FCSTD DOCUMENT  (FreeCAD 1.0R38641 +468 (Git))
Label: 03deltabot_assembly
License: All rights reserved
LicenseURL: https://en.wikipedia.org/wiki/All_rights_reserved
objects: App::FeaturePython×31, App::Link×23, Assembly::JointGroup×1, Assembly::AssemblyObject×1
EXTERNAL_REF file=01main.FCStd obj=Body004
EXTERNAL_REF file=01main.FCStd obj=Body006
EXTERNAL_REF file=01main.FCStd obj=Body007
EXTERNAL_REF file=stepper-motor-nema-23-57bygh201-1.snapshot.3/nema23.FCStd obj=Fusion001
EXTERNAL_REF file=01main.FCStd obj=Body008
EXTERNAL_REF file=si8t-k-rod-end-bearing-1.snapshot.1/8mm_rodend.FCStd obj=Part__Feature
EXTERNAL_REF file=01main.FCStd obj=Body
EXTERNAL_REF file=01main.FCStd obj=Body009

FEATURE [App::Link] base_triangle
  LinkedObject = -> <external 01main.FCStd>#Body004
FEATURE [App::FeaturePython] GroundedJoint  # Assembly grounded joint (typed FeaturePython)
  ObjectToGround = -> base_triangle
FEATURE [App::Link] vslot
  LinkPlacement = pos=(-30.6697,-27.5,-10.5) rot=(0,1,0;1.5708rad)
  LinkedObject = -> <external 01main.FCStd>#Body006
  Placement = pos=(-30.6697,-27.5,-10.5) rot=(0,1,0;1.5708rad)
FEATURE [App::FeaturePython] Joint  label="Slider"  # Assembly joint (typed FeaturePython)
  Activated = true
  AngleMax = 0
  AngleMin = 0
  Detach1 = false
  Detach2 = false
  Distance = 0
  Distance2 = 0
  EnableAngleMax = false
  EnableAngleMin = false
  EnableLengthMax = false
  EnableLengthMin = false
  JointType = 3 (Slider)
  LengthMax = 0
  LengthMin = 0
  Offset1 = pos=(-2,0,77) rot=(0,0,1;0rad)
  Offset2 = pos=(0,0,0) rot=(0,0,1;3.14159rad)
  Placement1 = pos=(-10.5,-10,180.895) rot=(0,0,1;0rad)
  Placement2 = pos=(1.22e-14,-37.5,0) rot=(0,-1,0;4.71239rad)
  Reference1 = -> Assembly [vslot.Edge5,vslot.Edge5]
  Reference2 = -> Assembly [base_triangle.Edge6,base_triangle.Edge6]
FEATURE [App::Link] nema23_holder
  LinkPlacement = pos=(145.212,-12,-49.5) rot=(1,0,0;1.5708rad)
  LinkedObject = -> <external 01main.FCStd>#Body007
  Placement = pos=(145.212,-12,-49.5) rot=(1,0,0;1.5708rad)
FEATURE [App::FeaturePython] Joint001  label="Slider001"  # Assembly joint (typed FeaturePython)
  Activated = true
  AngleMax = 0
  AngleMin = 0
  Detach1 = false
  Detach2 = false
  Distance = 0
  Distance2 = 0
  EnableAngleMax = false
  EnableAngleMin = false
  EnableLengthMax = false
  EnableLengthMin = false
  JointType = 3 (Slider)
  LengthMax = 0
  LengthMin = 0
  Offset1 = pos=(-2,-3,-72) rot=(0,0,1;0rad)
  Offset2 = pos=(0,0,0) rot=(0,0,1;1.5708rad)
  Placement1 = pos=(72,49,7) rot=(-0.707107,0,0.707107;3.14159rad)
  Placement2 = pos=(-10,8.5,103.895) rot=(0,0,1;1.5708rad)
  Reference1 = -> Assembly [nema23_holder.Edge21,nema23_holder.Edge21]
  Reference2 = -> Assembly [vslot.Edge113,vslot.Edge113]
FEATURE [App::Link] Fusion001
  LinkPlacement = pos=(145.212,-17,-49.5) rot=(1,0,0;4.71239rad)
  LinkedObject = -> <external stepper-motor-nema-23-57bygh201-1.snapshot.3/nema23.FCStd>#Fusion001
  Placement = pos=(145.212,-17,-49.5) rot=(1,0,0;4.71239rad)
FEATURE [App::FeaturePython] Joint002  label="Fixed"  # Assembly joint (typed FeaturePython)
  Activated = true
  AngleMax = 0
  AngleMin = 0
  Detach1 = false
  Detach2 = false
  Distance = 0
  Distance2 = 0
  EnableAngleMax = false
  EnableAngleMin = false
  EnableLengthMax = false
  EnableLengthMin = false
  JointType = 0 (Fixed)
  LengthMax = 0
  LengthMin = 0
  Placement1 = pos=(2.84e-14,0,5) rot=(0,0,1;0rad)
  Reference1 = -> Assembly [nema23_holder.Edge25,nema23_holder.Edge25]
  Reference2 = -> Assembly [Fusion001.Edge2256,Fusion001.Edge2256]
FEATURE [App::Link] bicep001
  LinkPlacement = pos=(145.212,-6,-49.5) rot=(0.724362,0.487494,0.487494;4.39537rad)
  LinkedObject = -> <external 01main.FCStd>#Body008
  Placement = pos=(145.212,-6,-49.5) rot=(0.724362,0.487494,0.487494;4.39537rad)
FEATURE [App::FeaturePython] Joint003  label="Revolute"  # Assembly joint (typed FeaturePython)
  Activated = true
  AngleMax = 34.3
  AngleMin = -61.59
  Detach1 = false
  Detach2 = false
  Distance = 0
  Distance2 = 0
  EnableAngleMax = false
  EnableAngleMin = false
  EnableLengthMax = false
  EnableLengthMin = false
  JointType = 1 (Revolute)
  LengthMax = 0
  LengthMin = 0
  Placement1 = pos=(0,7.1e-15,21) rot=(-1,0,0;3.14159rad)
  Placement2 = pos=(2.84e-14,0,10) rot=(0,0,1;0rad)
  Reference1 = -> Assembly [Fusion001.Edge2765,Fusion001.Edge2765]
  Reference2 = -> Assembly [bicep001.Edge21,bicep001.Edge21]
FEATURE [App::Link] vslot001
  LinkPlacement = pos=(0.572518,-1.79163,20) rot=(0.935113,0.250563,0.250563;1.63783rad)
  LinkedObject = -> <external 01main.FCStd>#Body006
  Placement = pos=(0.572518,-1.79163,20) rot=(0.935113,0.250563,0.250563;1.63783rad)
FEATURE [App::FeaturePython] Joint004  label="Slider002"  # Assembly joint (typed FeaturePython)
  Activated = true
  AngleMax = 0
  AngleMin = 0
  Detach1 = false
  Detach2 = false
  Distance = 0
  Distance2 = 0
  EnableAngleMax = false
  EnableAngleMin = false
  EnableLengthMax = false
  EnableLengthMin = false
  JointType = 3 (Slider)
  LengthMax = 0
  LengthMin = 0
  Offset1 = pos=(3,0,0) rot=(0,0,1;0rad)
  Offset2 = pos=(0,0,0) rot=(0,0,1;3.14159rad)
  Placement1 = pos=(5.77241,-20.9981,0) rot=(0.186157,-0.694747,0.694747;3.50969rad)
  Placement2 = pos=(-5.1,-10,103.895) rot=(0,0,1;3.14159rad)
  Reference1 = -> Assembly [base_triangle.Sketch020.Edge10,base_triangle.Sketch020.Edge10]
  Reference2 = -> Assembly [vslot001.Edge8,vslot001.Edge8]
FEATURE [App::Link] vslot002
  LinkPlacement = pos=(108.165,188.547,20) rot=(0.935113,-0.250563,-0.250563;1.63783rad)
  LinkedObject = -> <external 01main.FCStd>#Body006
  Placement = pos=(108.165,188.547,20) rot=(0.935113,-0.250563,-0.250563;1.63783rad)
FEATURE [App::FeaturePython] Joint005  label="Slider003"  # Assembly joint (typed FeaturePython)
  Activated = true
  AngleMax = 0
  AngleMin = 0
  Detach1 = false
  Detach2 = false
  Distance = 0
  Distance2 = 0
  EnableAngleMax = false
  EnableAngleMin = false
  EnableLengthMax = false
  EnableLengthMin = false
  JointType = 3 (Slider)
  LengthMax = 0
  LengthMin = 0
  Offset1 = pos=(0,-2,0) rot=(0,0,1;0rad)
  Placement1 = pos=(3.1,-10,103.895) rot=(0,0,1;0rad)
  Placement2 = pos=(12.7006,16.9981,0) rot=(-0.935113,0.250563,-0.250563;1.63783rad)
  Reference1 = -> Assembly [vslot002.Edge32,vslot002.Edge32]
  Reference2 = -> Assembly [base_triangle.Sketch020.Edge14,base_triangle.Sketch020.Edge14]
FEATURE [App::Link] vslot003
  LinkPlacement = pos=(-10.6404,0.6,21) rot=(0,1,0;4.71239rad)
  LinkedObject = -> <external 01main.FCStd>#Body006
  Placement = pos=(-10.6404,0.6,21) rot=(0,1,0;4.71239rad)
FEATURE [App::FeaturePython] Joint006  label="Slider004"  # Assembly joint (typed FeaturePython)
  Activated = true
  AngleMax = 0
  AngleMin = 0
  Detach1 = false
  Detach2 = false
  Distance = 0
  Distance2 = 0
  EnableAngleMax = false
  EnableAngleMin = false
  EnableLengthMax = false
  EnableLengthMin = false
  JointType = 3 (Slider)
  LengthMax = 0
  LengthMin = 0
  Offset1 = pos=(-3,0,0) rot=(0,0,1;0rad)
  Placement1 = pos=(-11,-3.1,103.895) rot=(0,0,1;0rad)
  Placement2 = pos=(-21.0711,-2.5,0) rot=(0.707107,0,0.707107;3.14159rad)
  Reference1 = -> Assembly [vslot003.Edge140,vslot003.Edge140]
  Reference2 = -> Assembly [base_triangle.Sketch020.Edge6,base_triangle.Sketch020.Edge6]
FEATURE [App::Link] vslot004
  LinkPlacement = pos=(110.289,-190.084,29.8935) rot=(0.965926,0.258819,0;3.14159rad)
  LinkedObject = -> <external 01main.FCStd>#Body006
  Placement = pos=(110.289,-190.084,29.8935) rot=(0.965926,0.258819,0;3.14159rad)
FEATURE [App::FeaturePython] Joint007  label="Perpendicular"  # Assembly joint (typed FeaturePython)
  Activated = true
  AngleMax = 0
  AngleMin = 0
  Detach1 = false
  Detach2 = false
  Distance = 0
  Distance2 = 0
  EnableAngleMax = false
  EnableAngleMin = false
  EnableLengthMax = false
  EnableLengthMin = false
  JointType = 7 (Perpendicular)
  LengthMax = 0
  LengthMin = 0
  Placement1 = pos=(6.8,-10,103.895) rot=(-1,0,0;1.5708rad)
  Placement2 = pos=(1.12e-14,-1.78e-14,207.79) rot=(0,0,1;0rad)
  Reference1 = -> Assembly [vslot004.Face13,vslot004.Face13]
  Reference2 = -> Assembly [vslot001.Face50,vslot001.Face50]
FEATURE [App::FeaturePython] GroundedJoint002  # Assembly grounded joint (typed FeaturePython)
  ObjectToGround = -> vslot001
FEATURE [App::Link] vslot005
  LinkPlacement = pos=(113.296,196.756,-177.874) rot=(0,0,1;4.18879rad)
  LinkedObject = -> <external 01main.FCStd>#Body006
  Placement = pos=(113.296,196.756,-177.874) rot=(0,0,1;4.18879rad)
FEATURE [App::FeaturePython] Joint008  label="Perpendicular001"  # Assembly joint (typed FeaturePython)
  Activated = true
  AngleMax = 0
  AngleMin = 0
  Detach1 = false
  Detach2 = false
  Distance = 0
  Distance2 = 0
  EnableAngleMax = false
  EnableAngleMin = false
  EnableLengthMax = false
  EnableLengthMin = false
  JointType = 7 (Perpendicular)
  LengthMax = 0
  LengthMin = 0
  Placement1 = pos=(4,0,103.895) rot=(0.57735,0.57735,-0.57735;4.18879rad)
  Reference1 = -> Assembly [vslot005.Face20,vslot005.Face20]
  Reference2 = -> Assembly [vslot002.Face49,vslot002.Face49]
FEATURE [App::FeaturePython] GroundedJoint003  # Assembly grounded joint (typed FeaturePython)
  ObjectToGround = -> vslot005
FEATURE [App::FeaturePython] GroundedJoint004  # Assembly grounded joint (typed FeaturePython)
  ObjectToGround = -> vslot002
FEATURE [App::FeaturePython] GroundedJoint005  # Assembly grounded joint (typed FeaturePython)
  ObjectToGround = -> vslot004
FEATURE [App::Link] vslot006
  LinkPlacement = pos=(-227.958,0.367079,-176.934) rot=(0,0,1;0rad)
  LinkedObject = -> <external 01main.FCStd>#Body006
  Placement = pos=(-227.958,0.367079,-176.934) rot=(0,0,1;0rad)
FEATURE [App::FeaturePython] GroundedJoint006  # Assembly grounded joint (typed FeaturePython)
  ObjectToGround = -> vslot006
FEATURE [App::Link] vslot007
  LinkPlacement = pos=(32.9973,-15.153,-11.7272) rot=(-0.186157,0.694747,0.694747;3.50969rad)
  LinkedObject = -> <external 01main.FCStd>#Body006
  Placement = pos=(32.9973,-15.153,-11.7272) rot=(-0.186157,0.694747,0.694747;3.50969rad)
FEATURE [App::FeaturePython] Joint009  label="Slider005"  # Assembly joint (typed FeaturePython)
  Activated = true
  AngleMax = 0
  AngleMin = 0
  Detach1 = false
  Detach2 = false
  Distance = 0
  Distance2 = 0
  EnableAngleMax = false
  EnableAngleMin = false
  EnableLengthMax = false
  EnableLengthMin = false
  JointType = 3 (Slider)
  LengthMax = 0
  LengthMin = 0
  Offset1 = pos=(0,9,-76) rot=(0,0,1;0rad)
  Placement1 = pos=(-15.4861,76.8227,-9) rot=(0.186157,-0.694747,0.694747;3.50969rad)
  Placement2 = pos=(-4,2.72721,103.895) rot=(0,0,1;0rad)
  Reference1 = -> Assembly [base_triangle.Edge39,base_triangle.Edge39]
  Reference2 = -> Assembly [vslot007.Edge128,vslot007.Edge128]
FEATURE [App::Link] vslot008
  LinkPlacement = pos=(-12.304,36.6889,-10.2728) rot=(0.935113,-0.250563,-0.250563;1.63783rad)
  LinkedObject = -> <external 01main.FCStd>#Body006
  Placement = pos=(-12.304,36.6889,-10.2728) rot=(0.935113,-0.250563,-0.250563;1.63783rad)
FEATURE [App::FeaturePython] Joint010  label="Slider006"  # Assembly joint (typed FeaturePython)
  Activated = true
  AngleMax = 0
  AngleMin = 0
  Detach1 = false
  Detach2 = false
  Distance = 0
  Distance2 = 0
  EnableAngleMax = false
  EnableAngleMin = false
  EnableLengthMax = false
  EnableLengthMin = false
  JointType = 3 (Slider)
  LengthMax = 0
  LengthMin = 0
  Offset1 = pos=(0,13,-80) rot=(0,0,1;0rad)
  Placement1 = pos=(4,10.2728,23.895) rot=(0,0,1;0rad)
  Placement2 = pos=(-20.7874,13.9952,0) rot=(-0.935113,0.250563,-0.250563;1.63783rad)
  Reference1 = -> Assembly [vslot008.Edge56,vslot008.Edge56]
  Reference2 = -> Assembly [base_triangle.Edge30,base_triangle.Edge30]
FEATURE [App::Link] nema23_holder001
  LinkPlacement = pos=(-63.6967,132.326,-49.2272) rot=(0.774597,-0.447214,-0.447214;1.82348rad)
  LinkedObject = -> <external 01main.FCStd>#Body007
  Placement = pos=(-63.6967,132.326,-49.2272) rot=(0.774597,-0.447214,-0.447214;1.82348rad)
FEATURE [App::FeaturePython] Joint011  label="Slider007"  # Assembly joint (typed FeaturePython)
  Activated = true
  AngleMax = 0
  AngleMin = 0
  Detach1 = false
  Detach2 = false
  Distance = 0
  Distance2 = 0
  EnableAngleMax = false
  EnableAngleMin = false
  EnableLengthMax = false
  EnableLengthMin = false
  JointType = 3 (Slider)
  LengthMax = 0
  LengthMin = 0
  Offset2 = pos=(0,0,0) rot=(0,0,1;3.14159rad)
  Placement1 = pos=(10,8.5,103.895) rot=(0,0,1;0rad)
  Placement2 = pos=(2.84e-14,46,5.3e-15) rot=(0,1,0;4.71239rad)
  Reference1 = -> Assembly [vslot007.Edge74,vslot007.Edge74]
  Reference2 = -> Assembly [nema23_holder001.Edge6,nema23_holder001.Edge6]
FEATURE [App::Link] nema23_holder002
  LinkPlacement = pos=(-91.6035,-120.662,-47.7728) rot=(0.774597,0.447214,0.447214;1.82348rad)
  LinkedObject = -> <external 01main.FCStd>#Body007
  Placement = pos=(-91.6035,-120.662,-47.7728) rot=(0.774597,0.447214,0.447214;1.82348rad)
FEATURE [App::FeaturePython] Joint012  label="Slider008"  # Assembly joint (typed FeaturePython)
  Activated = true
  AngleMax = 0
  AngleMin = 0
  Detach1 = false
  Detach2 = false
  Distance = 0
  Distance2 = 0
  EnableAngleMax = false
  EnableAngleMin = false
  EnableLengthMax = false
  EnableLengthMin = false
  JointType = 3 (Slider)
  LengthMax = 0
  LengthMin = 0
  Offset2 = pos=(0,0,0) rot=(0,0,1;3.14159rad)
  Placement1 = pos=(10,8.5,103.895) rot=(0,0,1;0rad)
  Placement2 = pos=(2.84e-14,46,0) rot=(0,1,0;4.71239rad)
  Reference1 = -> Assembly [vslot008.Edge74,vslot008.Edge74]
  Reference2 = -> Assembly [nema23_holder002.Edge6,nema23_holder002.Edge6]
FEATURE [App::Link] Fusion002
  LinkPlacement = pos=(-63.6967,132.326,-49.2272) rot=(0.774597,-0.447214,-0.447214;1.82348rad)
  LinkedObject = -> <external stepper-motor-nema-23-57bygh201-1.snapshot.3/nema23.FCStd>#Fusion001
  Placement = pos=(-63.6967,132.326,-49.2272) rot=(0.774597,-0.447214,-0.447214;1.82348rad)
FEATURE [App::FeaturePython] Joint013  label="Fixed001"  # Assembly joint (typed FeaturePython)
  Activated = true
  AngleMax = 0
  AngleMin = 0
  Detach1 = false
  Detach2 = false
  Distance = 0
  Distance2 = 0
  EnableAngleMax = false
  EnableAngleMin = false
  EnableLengthMax = false
  EnableLengthMin = false
  JointType = 0 (Fixed)
  LengthMax = 0
  LengthMin = 0
  Reference1 = -> Assembly [Fusion002.Edge2256,Fusion002.Edge2256]
  Reference2 = -> Assembly [nema23_holder001.Edge10,nema23_holder001.Edge10]
FEATURE [App::Link] Fusion003
  LinkPlacement = pos=(-91.6035,-120.662,-47.7728) rot=(0.774597,0.447214,0.447214;1.82348rad)
  LinkedObject = -> <external stepper-motor-nema-23-57bygh201-1.snapshot.3/nema23.FCStd>#Fusion001
  Placement = pos=(-91.6035,-120.662,-47.7728) rot=(0.774597,0.447214,0.447214;1.82348rad)
FEATURE [App::FeaturePython] Joint014  label="Fixed002"  # Assembly joint (typed FeaturePython)
  Activated = true
  AngleMax = 0
  AngleMin = 0
  Detach1 = false
  Detach2 = false
  Distance = 0
  Distance2 = 0
  EnableAngleMax = false
  EnableAngleMin = false
  EnableLengthMax = false
  EnableLengthMin = false
  JointType = 0 (Fixed)
  LengthMax = 0
  LengthMin = 0
  Reference1 = -> Assembly [Fusion003.Edge2256,Fusion003.Edge2256]
  Reference2 = -> Assembly [nema23_holder002.Edge10,nema23_holder002.Edge10]
FEATURE [App::Link] SI8T_K_Rod_End_Bearing_v2  label="SI8T/K Rod End Bearing v2"
  LinkPlacement = pos=(220.519,-12,135.781) rot=(-0.57735,0.57735,0.57735;4.18879rad)
  LinkedObject = -> <external si8t-k-rod-end-bearing-1.snapshot.1/8mm_rodend.FCStd>#Part__Feature
  Placement = pos=(220.519,-12,135.781) rot=(-0.57735,0.57735,0.57735;4.18879rad)
FEATURE [App::FeaturePython] Joint015  label="Revolute001"  # Assembly joint (typed FeaturePython)
  Activated = true
  AngleMax = 0
  AngleMin = 0
  Detach1 = false
  Detach2 = false
  Distance = 0
  Distance2 = 0
  EnableAngleMax = false
  EnableAngleMin = false
  EnableLengthMax = false
  EnableLengthMin = false
  JointType = 1 (Revolute)
  LengthMax = 0
  LengthMin = 0
  Placement1 = pos=(-6,0,-2.84e-14) rot=(-0.707107,0,-0.707107;3.14159rad)
  Placement2 = pos=(200,0,9e-16) rot=(0,0,1;0rad)
  Reference1 = -> Assembly [SI8T_K_Rod_End_Bearing_v2.Edge108,SI8T_K_Rod_End_Bearing_v2.Edge108]
  Reference2 = -> Assembly [bicep001.Edge18,bicep001.Edge18]
FEATURE [App::Link] SI8T_K_Rod_End_Bearing_v003  label="SI8T/K Rod End Bearing v003"
  LinkPlacement = pos=(220.519,10,135.781) rot=(0.57735,0.57735,-0.57735;4.18879rad)
  LinkedObject = -> <external si8t-k-rod-end-bearing-1.snapshot.1/8mm_rodend.FCStd>#Part__Feature
  Placement = pos=(220.519,10,135.781) rot=(0.57735,0.57735,-0.57735;4.18879rad)
FEATURE [App::FeaturePython] Joint016  label="Revolute002"  # Assembly joint (typed FeaturePython)
  Activated = true
  AngleMax = 0
  AngleMin = 0
  Detach1 = false
  Detach2 = false
  Distance = 0
  Distance2 = 0
  EnableAngleMax = false
  EnableAngleMin = false
  EnableLengthMax = false
  EnableLengthMin = false
  JointType = 1 (Revolute)
  LengthMax = 0
  LengthMin = 0
  Placement1 = pos=(200,2.84e-14,10) rot=(0,0,1;0rad)
  Placement2 = pos=(-6,0,0) rot=(-0.707107,0,-0.707107;3.14159rad)
  Reference1 = -> Assembly [bicep001.Edge24,bicep001.Edge24]
  Reference2 = -> Assembly [SI8T_K_Rod_End_Bearing_v003.Edge108,SI8T_K_Rod_End_Bearing_v003.Edge108]
FEATURE [App::Link] forearm_axis
  LinkPlacement = pos=(220.519,10,-100.519) rot=(0,0,1;3.14159rad)
  LinkedObject = -> <external 01main.FCStd>#Body
  Placement = pos=(220.519,10,-100.519) rot=(0,0,1;3.14159rad)
FEATURE [App::Link] forearm_axis001
  LinkPlacement = pos=(220.519,-12,-27.9194) rot=(0,0,1;0rad)
  LinkedObject = -> <external 01main.FCStd>#Body
  Placement = pos=(220.519,-12,-27.9194) rot=(0,0,1;0rad)
FEATURE [App::FeaturePython] Joint018  label="Fixed003"  # Assembly joint (typed FeaturePython)
  Activated = true
  AngleMax = 0
  AngleMin = 0
  Detach1 = false
  Detach2 = false
  Distance = 0
  Distance2 = 0
  EnableAngleMax = false
  EnableAngleMin = false
  EnableLengthMax = false
  EnableLengthMin = false
  JointType = 0 (Fixed)
  LengthMax = 0
  LengthMin = 0
  Placement1 = pos=(0,0,200) rot=(0,0,1;0rad)
  Placement2 = pos=(-7.1e-15,36.3,2.84e-14) rot=(-0.57735,-0.57735,-0.57735;2.0944rad)
  Reference1 = -> Assembly [forearm_axis001.Edge3,forearm_axis001.Edge3]
  Reference2 = -> Assembly [SI8T_K_Rod_End_Bearing_v2.Edge3,SI8T_K_Rod_End_Bearing_v2.Edge3]
FEATURE [App::FeaturePython] Joint019  label="Fixed004"  # Assembly joint (typed FeaturePython)
  Activated = true
  AngleMax = 0
  AngleMin = 0
  Detach1 = false
  Detach2 = false
  Distance = 0
  Distance2 = 0
  EnableAngleMax = false
  EnableAngleMin = false
  EnableLengthMax = false
  EnableLengthMin = false
  JointType = 0 (Fixed)
  LengthMax = 0
  LengthMin = 0
  Placement1 = pos=(0,1.8e-15,200) rot=(0,0,1;0rad)
  Placement2 = pos=(-7.1e-15,36.3,0) rot=(-0.57735,-0.57735,-0.57735;2.0944rad)
  Reference1 = -> Assembly [forearm_axis.Edge3,forearm_axis.Edge3]
  Reference2 = -> Assembly [SI8T_K_Rod_End_Bearing_v003.Edge3,SI8T_K_Rod_End_Bearing_v003.Edge3]
FEATURE [App::FeaturePython] Joint020  label="Parallel"  # Assembly joint (typed FeaturePython)
  Activated = true
  AngleMax = 0
  AngleMin = 0
  Detach1 = false
  Detach2 = false
  Distance = 0
  Distance2 = 0
  EnableAngleMax = false
  EnableAngleMin = false
  EnableLengthMax = false
  EnableLengthMin = false
  JointType = 6 (Parallel)
  LengthMax = 0
  LengthMin = 0
  Reference1 = -> Assembly [forearm_axis001.Face1,forearm_axis001.Face1]
  Reference2 = -> Assembly [forearm_axis.Face1,forearm_axis.Face1]
FEATURE [App::Link] tool001
  LinkPlacement = pos=(177.519,24.0451,-271.719) rot=(0,0,1;0.523599rad)
  LinkedObject = -> <external 01main.FCStd>#Body009
  Placement = pos=(177.519,24.0451,-271.719) rot=(0,0,1;0.523599rad)
FEATURE [App::FeaturePython] Joint021  label="Parallel001"  # Assembly joint (typed FeaturePython)
  Activated = true
  AngleMax = 0
  AngleMin = 0
  Detach1 = false
  Detach2 = false
  Distance = 0
  Distance2 = 0
  EnableAngleMax = false
  EnableAngleMin = false
  EnableLengthMax = false
  EnableLengthMin = false
  JointType = 6 (Parallel)
  LengthMax = 0
  LengthMin = 0
  Placement1 = pos=(2e-16,-1.76e-14,0) rot=(0,0,1;0rad)
  Placement2 = pos=(-43.3013,-25,7.5) rot=(-0.377964,-0.654654,0.654654;2.41886rad)
  Reference1 = -> Assembly [base_triangle.Face4,base_triangle.Face4]
  Reference2 = -> Assembly [tool001.Face9,tool001.Face9]
FEATURE [App::FeaturePython] Joint022  label="Perpendicular002"  # Assembly joint (typed FeaturePython)
  Activated = true
  AngleMax = 0
  AngleMin = 0
  Detach1 = false
  Detach2 = false
  Distance = 0
  Distance2 = 0
  EnableAngleMax = false
  EnableAngleMin = false
  EnableLengthMax = false
  EnableLengthMin = false
  JointType = 7 (Perpendicular)
  LengthMax = 0
  LengthMin = 0
  Placement1 = pos=(4,0,2.84e-14) rot=(0,0,1;0rad)
  Placement2 = pos=(-37.2391,-21.5,5.68e-14) rot=(-0.935113,-0.250563,0.250563;1.63783rad)
  Reference1 = -> Assembly [forearm_axis.Edge1,forearm_axis.Edge1]
  Reference2 = -> Assembly [tool001.Edge18,tool001.Edge18]
FEATURE [App::FeaturePython] GroundedJoint007  # Assembly grounded joint (typed FeaturePython)
  ObjectToGround = -> nema23_holder
FEATURE [App::Link] SI8T_K_Rod_End_Bearing_v004  label="SI8T/K Rod End Bearing v004"
  LinkPlacement = pos=(220.519,-12,-264.219) rot=(0.57735,0.57735,0.57735;2.0944rad)
  LinkedObject = -> <external si8t-k-rod-end-bearing-1.snapshot.1/8mm_rodend.FCStd>#Part__Feature
  Placement = pos=(220.519,-12,-264.219) rot=(0.57735,0.57735,0.57735;2.0944rad)
FEATURE [App::FeaturePython] Joint023  label="Fixed005"  # Assembly joint (typed FeaturePython)
  Activated = true
  AngleMax = 0
  AngleMin = 0
  Detach1 = false
  Detach2 = false
  Distance = 0
  Distance2 = 0
  EnableAngleMax = false
  EnableAngleMin = false
  EnableLengthMax = false
  EnableLengthMin = false
  JointType = 0 (Fixed)
  LengthMax = 0
  LengthMin = 0
  Placement1 = pos=(-1.07e-14,36.3,0) rot=(-0.57735,-0.57735,-0.57735;2.0944rad)
  Placement2 = pos=(0,0,-200) rot=(0,0,1;0rad)
  Reference1 = -> Assembly [SI8T_K_Rod_End_Bearing_v004.Edge3,SI8T_K_Rod_End_Bearing_v004.Edge3]
  Reference2 = -> Assembly [forearm_axis001.Edge2,forearm_axis001.Edge2]
FEATURE [App::FeaturePython] Joint024  label="Cylindrical"  # Assembly joint (typed FeaturePython)
  Activated = true
  AngleMax = 0
  AngleMin = 0
  Detach1 = false
  Detach2 = false
  Distance = 0
  Distance2 = 0
  EnableAngleMax = false
  EnableAngleMin = false
  EnableLengthMax = false
  EnableLengthMin = false
  JointType = 2 (Cylindrical)
  LengthMax = 0
  LengthMin = 0
  Placement1 = pos=(-1.8e-15,0,0) rot=(0,-1,0;1.5708rad)
  Placement2 = pos=(37.2391,-21.5,7.5) rot=(0.935113,-0.250563,-0.250563;1.63783rad)
  Reference1 = -> Assembly [SI8T_K_Rod_End_Bearing_v004.Face45,SI8T_K_Rod_End_Bearing_v004.Face45]
  Reference2 = -> Assembly [tool001.Face10,tool001.Face10]
FEATURE [Assembly::JointGroup] Joints
  Group = -> [GroundedJoint,Joint,Joint001,Joint002,Joint003,Joint004,Joint005,Joint006,Joint007,GroundedJoint002,Joint008,GroundedJoint003,GroundedJoint004,GroundedJoint005,GroundedJoint006,Joint009,Joint010,Joint011,Joint012,Joint013,Joint014,Joint015,Joint016,Joint018,Joint019,Joint020,Joint021,Joint022,GroundedJoint007,Joint023,Joint024]
FEATURE [Assembly::AssemblyObject] Assembly
  Group = -> [Joints,base_triangle,GroundedJoint,vslot,Joint,nema23_holder,Joint001,Fusion001,Joint002,bicep001,Joint003,vslot001,Joint004,vslot002,Joint005,vslot003,Joint006,vslot004,Joint007,GroundedJoint002,vslot005,Joint008,GroundedJoint003,GroundedJoint004,GroundedJoint005,vslot006,GroundedJoint006,vslot007,Joint009,vslot008,Joint010,nema23_holder001,Joint011,nema23_holder002,Joint012,Fusion002,Joint013,+18 more]
  Origin = -> Origin
  Type = Assembly

RESOLVED EXTERNAL PARTS (link-assembly join: the EXTERNAL_REF files above that resolve inside this repo's crawl, each included once):
---- part 01main.FCStd = doc fcstd_2c6c7f2358a4 ----
FCSTD DOCUMENT  (FreeCAD 1.0R38641 +468 (Git))
Label: 01main
License: All rights reserved
LicenseURL: https://en.wikipedia.org/wiki/All_rights_reserved
objects: Sketcher::SketchObject×14, PartDesign::Body×7, PartDesign::Pad×6, App::Part×4, PartDesign::Pocket×4, PartDesign::PolarPattern×3, PartDesign::Fillet×2, Spreadsheet::Sheet×1, PartDesign::Hole×1, PartDesign::Chamfer×1, PartDesign::Revolution×1, Part::Part2DObjectPython×1
note: 87 computed .brp shape members not serialized (recipe doc carries the construction recipe); baked Part::Feature solids carry a one-line shape summary decoded from their .brp

FEATURE [Spreadsheet::Sheet] Spreadsheet  label="ss"
  cells = A1='deltabot calculation - values for kinetic | https://www.marginallyclever.com/other/samples/fk-ik-test.html; A3='Base radius (f); B3(f)=300; D3='vslot_length-28.5!; E3==<<base_triangle_sketch>>.Constraints.vslot_length; F3='28.5 to add (halt nema 23); A4='Bicep length (rf); B4(rf)=200; C4='!= tube actual length; E4(vslot_length)==179.29 + 28.5; A5='Bicep inerdia (od_rf); B5(od_rf)=40; A6='Bicep outerdia (id_rf); B6(id_rf)=36; D6='DELTA_F; E6==<<Sketch024>>.Constraints.DELTA_F; A7='Bicep end length (end_rf); B7(end_rf)=25; A11='Forearm length (re); B11(re)=400; A12='End Effector radius (e); A13='Base to floor distance (b); A14='wrist(tool); B14(wrist)=90
FEATURE [Sketcher::SketchObject] Sketch
  ArcFitTolerance = 0
  AttachmentSupport = -> [XY_Plane]
  FullyConstrained = true
  MakeInternals = false
  MapMode = 5
  sketch-geometry (1):
    g0: Circle CenterX=0 CenterY=0 CenterZ=0 NormalX=0 NormalY=0 NormalZ=1 AngleXU=0 Radius=4
  constraints (2):
    c: Coincident(g0,g-1)
    c: Diameter(g0) = 8
FEATURE [App::Part] Part002  label="tool"
  Origin = -> Origin010
FEATURE [Sketcher::SketchObject] Sketch010
  ArcFitTolerance = 1e-06
  AttachmentSupport = -> [XY_Plane011]
  FullyConstrained = true
  MakeInternals = false
  MapMode = 5
FEATURE [Sketcher::SketchObject] Sketch011  label="base_triangle_sketch"
  ArcFitTolerance = 1e-06
  AttachmentSupport = -> [XY_Plane012]
  FullyConstrained = false
  MakeInternals = false
  MapMode = 5
  sketch-geometry (16):
    g0: Circle [constr] CenterX=0 CenterY=0 CenterZ=0 NormalX=0 NormalY=0 NormalZ=1 AngleXU=0 Radius=300
    g1: Circle [constr] CenterX=0 CenterY=0 CenterZ=0 NormalX=0 NormalY=0 NormalZ=1 AngleXU=0 Radius=110
    g2: LineSegment [constr] StartX=0 StartY=150 StartZ=0 EndX=-129.904 EndY=-75 EndZ=0
    g3: LineSegment [constr] StartX=-129.904 StartY=-75 StartZ=0 EndX=129.904 EndY=-75 EndZ=0
    g4: LineSegment [constr] StartX=129.904 StartY=-75 StartZ=0 EndX=0 EndY=150 EndZ=0
    g5: Circle [constr] CenterX=0 CenterY=0 CenterZ=0 NormalX=0 NormalY=0 NormalZ=1 AngleXU=0 Radius=150
    g6: LineSegment [constr] StartX=0 StartY=110 StartZ=0 EndX=195.089 EndY=-227.904 EndZ=0
    g7: LineSegment [constr] StartX=95.2628 StartY=-55 StartZ=0 EndX=-294.915 EndY=-55 EndZ=0
    g8: LineSegment [constr] StartX=-71.877 StartY=-83.2688 StartZ=0 EndX=67.7767 EndY=292.244 EndZ=0
    g9: LineSegment StartX=-51.5163 StartY=60.7711 StartZ=0 EndX=51.5163 EndY=60.7711 EndZ=0
    g10: LineSegment StartX=78.3875 StartY=14.2289 StartZ=0 EndX=26.8711 EndY=-75 EndZ=0
    g11: LineSegment StartX=-26.8711 StartY=-75 StartZ=0 EndX=-78.3875 EndY=14.2289 EndZ=0
    g12: LineSegment StartX=-51.5163 StartY=60.7711 StartZ=0 EndX=-78.3875 EndY=14.2289 EndZ=0
    g13: LineSegment StartX=-26.8711 StartY=-75 StartZ=0 EndX=26.8711 EndY=-75 EndZ=0
    g14: LineSegment StartX=51.5163 StartY=60.7711 StartZ=0 EndX=78.3875 EndY=14.2289 EndZ=0
    g15: LineSegment [constr] StartX=95.2628 StartY=-55 StartZ=0 EndX=112.583 EndY=-45 EndZ=0
  constraints (47):
    c: Coincident(g0,g-1)
    c: PointOnObject(g8,g1)
    c: PointOnObject(g7,g1)
    c: PointOnObject(g6,g1)
    c: Coincident(g1,g0)
    c: Coincident(g2,g3)
    c: Coincident(g3,g4)
    c: Coincident(g4,g2)
    c: Equal(g2,g3)
    c: Equal(g2,g4)
    c: PointOnObject(g2,g5)
    c: PointOnObject(g3,g5)
    c: PointOnObject(g4,g5)
    c: Coincident(g5,g0)
    c: PointOnObject(g6,g-2)
    c: PointOnObject(g2,g-2)
    c: PointOnObject(g6,g0)
    c: PointOnObject(g7,g6)
    c: PointOnObject(g7,g0)
    c: Horizontal(g7)
    c: PointOnObject(g6,g8)
    c: PointOnObject(g8,g0)
    c: Diameter(g5) = 300
    c: Distance(g6,g6) = 390.178  'vslot_length'
    c: PointOnObject(g9,g2)
    c: PointOnObject(g9,g4)
    c: Horizontal(g9)
    c: PointOnObject(g10,g4)
    c: PointOnObject(g10,g3)
    c: PointOnObject(g11,g3)
    c: PointOnObject(g11,g2)
    c: Coincident(g9,g12)
    c: Coincident(g12,g11)
    c: Coincident(g11,g13)
    c: Coincident(g13,g10)
    c: Coincident(g9,g14)
    c: Coincident(g14,g10)
    c: Equal(g13,g12)
    c: Equal(g12,g14)
    c: Angle(g13,g11) = 2.0944
    c: Angle(g10,g13) = 2.0944
    c: Parallel(g6,g14)
    c: Coincident(g15,g7)
    c: PointOnObject(g15,g4)
    c: Perpendicular(g6,g15)
    c: Distance(g15,g15) = 20
    c: Diameter(g0) = 600
FEATURE [PartDesign::Pad] Pad007
  Direction = (0,0,1)
  Length = 10
  Length2 = 10
  Profile = -> Sketch011
  ReferenceAxis = -> Sketch011 [N_Axis]
  Refine = true
  Suppressed = false
  Type = 0
FEATURE [Sketcher::SketchObject] Sketch015
  ArcFitTolerance = 1e-06
  AttachmentSupport = -> [XY_Plane014]
  FullyConstrained = false
  MakeInternals = false
  MapMode = 5
  sketch-geometry (50):
    g0: ArcOfCircle CenterX=0 CenterY=0 CenterZ=0 NormalX=0 NormalY=0 NormalZ=1 AngleXU=0 Radius=2.5 StartAngle=3.14159 EndAngle=6.28319
    g1: LineSegment StartX=-10 StartY=-5.1 StartZ=0 EndX=-10 EndY=-8.5 EndZ=0
    g2: ArcOfCircle CenterX=-8.5 CenterY=-8.5 CenterZ=0 NormalX=0 NormalY=0 NormalZ=1 AngleXU=0 Radius=1.5 StartAngle=3.14159 EndAngle=4.71239
    g3: LineSegment StartX=-8.5 StartY=-10 StartZ=0 EndX=-5.1 EndY=-10 EndZ=0
    g4: LineSegment StartX=-5.1 StartY=-10 StartZ=0 EndX=-3.1 EndY=-8 EndZ=0
    g5: LineSegment StartX=-3.1 StartY=-8 StartZ=0 EndX=-5.3 EndY=-8 EndZ=0
    g6: LineSegment StartX=-5.3 StartY=-8 StartZ=0 EndX=-5.3 EndY=-6.57279 EndZ=0
    g7: LineSegment StartX=-5.3 StartY=-6.57279 StartZ=0 EndX=-2.72721 EndY=-4 EndZ=0
    g8: LineSegment StartX=-2.72721 StartY=-4 StartZ=0 EndX=2.72721 EndY=-4 EndZ=0
    g9: LineSegment StartX=2.72721 StartY=-4 StartZ=0 EndX=5.3 EndY=-6.57279 EndZ=0
    g10: LineSegment StartX=5.3 StartY=-6.57279 StartZ=0 EndX=5.3 EndY=-8 EndZ=0
    g11: LineSegment StartX=5.3 StartY=-8 StartZ=0 EndX=3.1 EndY=-8 EndZ=0
    g12: LineSegment StartX=3.1 StartY=-8 StartZ=0 EndX=5.1 EndY=-10 EndZ=0
    g13: LineSegment StartX=5.1 StartY=-10 StartZ=0 EndX=8.5 EndY=-10 EndZ=0
    g14: ArcOfCircle CenterX=8.5 CenterY=-8.5 CenterZ=0 NormalX=0 NormalY=0 NormalZ=1 AngleXU=0 Radius=1.5 StartAngle=4.71239 EndAngle=6.28319
    g15: LineSegment StartX=10 StartY=-8.5 StartZ=0 EndX=10 EndY=-5.1 EndZ=0
    g16: LineSegment StartX=10 StartY=-5.1 StartZ=0 EndX=8 EndY=-3.1 EndZ=0
    g17: LineSegment StartX=8 StartY=-3.1 StartZ=0 EndX=8 EndY=-5.3 EndZ=0
    g18: LineSegment StartX=8 StartY=-5.3 StartZ=0 EndX=6.57279 EndY=-5.3 EndZ=0
    g19: LineSegment StartX=6.57279 StartY=-5.3 StartZ=0 EndX=4 EndY=-2.72721 EndZ=0
    g20: LineSegment StartX=4 StartY=-2.72721 StartZ=0 EndX=4 EndY=2.72721 EndZ=0
    g21: LineSegment StartX=4 StartY=2.72721 StartZ=0 EndX=6.57279 EndY=5.3 EndZ=0
    g22: LineSegment StartX=6.57279 StartY=5.3 StartZ=0 EndX=8 EndY=5.3 EndZ=0
    g23: LineSegment StartX=8 StartY=5.3 StartZ=0 EndX=8 EndY=3.1 EndZ=0
    g24: LineSegment StartX=8 StartY=3.1 StartZ=0 EndX=10 EndY=5.1 EndZ=0
    g25: LineSegment StartX=10 StartY=5.1 StartZ=0 EndX=10 EndY=8.5 EndZ=0
    g26: ArcOfCircle CenterX=8.5 CenterY=8.5 CenterZ=0 NormalX=0 NormalY=0 NormalZ=1 AngleXU=0 Radius=1.5 StartAngle=0 EndAngle=1.5708
    g27: LineSegment StartX=8.5 StartY=10 StartZ=0 EndX=5.1 EndY=10 EndZ=0
    g28: LineSegment StartX=5.1 StartY=10 StartZ=0 EndX=3.1 EndY=8 EndZ=0
    g29: LineSegment StartX=3.1 StartY=8 StartZ=0 EndX=5.3 EndY=8 EndZ=0
    g30: LineSegment StartX=5.3 StartY=8 StartZ=0 EndX=5.3 EndY=6.57279 EndZ=0
    g31: LineSegment StartX=5.3 StartY=6.57279 StartZ=0 EndX=2.72721 EndY=4 EndZ=0
    g32: LineSegment StartX=2.72721 StartY=4 StartZ=0 EndX=-2.72721 EndY=4 EndZ=0
    g33: LineSegment StartX=-2.72721 StartY=4 StartZ=0 EndX=-5.3 EndY=6.57279 EndZ=0
    g34: LineSegment StartX=-5.3 StartY=6.57279 StartZ=0 EndX=-5.3 EndY=8 EndZ=0
    g35: LineSegment StartX=-5.3 StartY=8 StartZ=0 EndX=-3.1 EndY=8 EndZ=0
    g36: LineSegment StartX=-3.1 StartY=8 StartZ=0 EndX=-5.1 EndY=10 EndZ=0
    g37: LineSegment StartX=-5.1 StartY=10 StartZ=0 EndX=-8.5 EndY=10 EndZ=0
    g38: ArcOfCircle CenterX=-8.5 CenterY=8.5 CenterZ=0 NormalX=0 NormalY=0 NormalZ=1 AngleXU=0 Radius=1.5 StartAngle=1.5708 EndAngle=3.14159
    g39: LineSegment StartX=-10 StartY=8.5 StartZ=0 EndX=-10 EndY=5.1 EndZ=0
    g40: LineSegment StartX=-10 StartY=5.1 StartZ=0 EndX=-8 EndY=3.1 EndZ=0
    g41: LineSegment StartX=-8 StartY=3.1 StartZ=0 EndX=-8 EndY=5.3 EndZ=0
    g42: LineSegment StartX=-8 StartY=5.3 StartZ=0 EndX=-6.57279 EndY=5.3 EndZ=0
    g43: LineSegment StartX=-6.57279 StartY=5.3 StartZ=0 EndX=-4 EndY=2.72721 EndZ=0
    g44: LineSegment StartX=-4 StartY=2.72721 StartZ=0 EndX=-4 EndY=-2.72721 EndZ=0
    g45: LineSegment StartX=-4 StartY=-2.72721 StartZ=0 EndX=-6.57279 EndY=-5.3 EndZ=0
    g46: LineSegment StartX=-6.57279 StartY=-5.3 StartZ=0 EndX=-8 EndY=-5.3 EndZ=0
    g47: LineSegment StartX=-8 StartY=-5.3 StartZ=0 EndX=-8 EndY=-3.1 EndZ=0
    g48: LineSegment StartX=-8 StartY=-3.1 StartZ=0 EndX=-10 EndY=-5.1 EndZ=0
    g49: ArcOfCircle CenterX=0 CenterY=0 CenterZ=0 NormalX=0 NormalY=0 NormalZ=1 AngleXU=0 Radius=2.5 StartAngle=0 EndAngle=3.14159
FEATURE [Sketcher::SketchObject] Sketch012
  ArcFitTolerance = 1e-06
  AttachmentSupport = -> [XY_Plane012]
  ExternalGeometry = -> [Pad007]
  FullyConstrained = true
  MakeInternals = false
  MapMode = 5
  sketch-geometry (7):
    g0: Circle CenterX=-35 CenterY=50.7711 CenterZ=0 NormalX=0 NormalY=0 NormalZ=1 AngleXU=0 Radius=2.5
    g1: LineSegment [constr] StartX=0 StartY=50.7711 StartZ=0 EndX=-35 EndY=50.7711 EndZ=0
    g2: Circle CenterX=35 CenterY=50.7711 CenterZ=0 NormalX=0 NormalY=0 NormalZ=1 AngleXU=0 Radius=2.5
    g3: ArcOfCircle [constr] CenterX=-35 CenterY=50.7711 CenterZ=0 NormalX=0 NormalY=0 NormalZ=1 AngleXU=0 Radius=2.6 StartAngle=1.5708 EndAngle=4.71239
    g4: ArcOfCircle [constr] CenterX=35 CenterY=50.7711 CenterZ=0 NormalX=0 NormalY=0 NormalZ=1 AngleXU=0 Radius=2.6 StartAngle=4.71239 EndAngle=7.85398
    g5: LineSegment [constr] StartX=-35 StartY=53.3711 StartZ=0 EndX=35 EndY=53.3711 EndZ=0
    g6: LineSegment [constr] StartX=-35 StartY=48.1711 StartZ=0 EndX=35 EndY=48.1711 EndZ=0
  constraints (16):
    c: Coincident(g0,g1)
    c: Symmetric(g0,g2,g1)
    c: Equal(g2,g0)
    c: Diameter(g0) = 5
    c: Distance(g0,g2) = 70
    c: Tangent(g3,g5) = 1.5708
    c: Tangent(g3,g6) = -1.5708
    c: Tangent(g4,g5) = 1.5708
    c: Tangent(g4,g6) = -1.5708
    c: Equal(g3,g4)
    c: Coincident(g3,g0)
    c: Coincident(g4,g2)
    c: Radius(g4) = 2.6
    c: PointOnObject(g1,g-2)
    c: Perpendicular(g-2,g1)
    c: DistanceY(g2,g-3) = 10
FEATURE [PartDesign::Pocket] Pocket003
  BaseFeature = -> Pad007
  Direction = (0,0,-1)
  Length = 5
  Length2 = 5
  Profile = -> Sketch012
  ReferenceAxis = -> Sketch012 [N_Axis]
  Refine = true
  Reversed = true
  Suppressed = false
  Type = 1
FEATURE [PartDesign::PolarPattern] PolarPattern
  Angle = 360
  Axis = -> Sketch012 [N_Axis]
  BaseFeature = -> Pocket003
  Mode = 0
  Occurrences = 3
  Offset = 120
  Originals = -> [Pocket003]
  Refine = true
  Suppressed = false
  TransformMode = 0
FEATURE [PartDesign::Pad] Pad008
  Direction = (0,0,1)
  Length = 207.79
  Length2 = 10
  Profile = -> Sketch015
  ReferenceAxis = -> Sketch015 [N_Axis]
  Refine = true
  Suppressed = false
  Type = 0
  expr: Length = <<ss>>.vslot_length
FEATURE [PartDesign::Body] Body006  label="vslot"
  AllowCompound = false
  Group = -> [Sketch015,Pad008]
  Origin = -> Origin024
  Tip = -> Pad008
FEATURE [Sketcher::SketchObject] Sketch016
  ArcFitTolerance = 1e-06
  AttachmentSupport = -> [XY_Plane015]
  FullyConstrained = false
  MakeInternals = false
  MapMode = 5
  sketch-geometry (19):
    g0: Circle CenterX=0 CenterY=0 CenterZ=0 NormalX=0 NormalY=0 NormalZ=1 AngleXU=0 Radius=20
    g1: LineSegment [constr] StartX=-23.5 StartY=-23.5 StartZ=0 EndX=23.5 EndY=-23.5 EndZ=0
    g2: LineSegment [constr] StartX=23.5 StartY=-23.5 StartZ=0 EndX=23.5 EndY=23.5 EndZ=0
    g3: LineSegment [constr] StartX=23.5 StartY=23.5 StartZ=0 EndX=-23.5 EndY=23.5 EndZ=0
    g4: LineSegment [constr] StartX=-23.5 StartY=23.5 StartZ=0 EndX=-23.5 EndY=-23.5 EndZ=0
    g5: GeomPoint [constr] X=0 Y=0 Z=0
    g6: Circle CenterX=-23.5 CenterY=23.5 CenterZ=0 NormalX=0 NormalY=0 NormalZ=1 AngleXU=0 Radius=2.5
    g7: Circle CenterX=23.5 CenterY=23.5 CenterZ=0 NormalX=0 NormalY=0 NormalZ=1 AngleXU=0 Radius=2.5
    g8: Circle CenterX=23.5 CenterY=-23.5 CenterZ=0 NormalX=0 NormalY=0 NormalZ=1 AngleXU=0 Radius=2.5
    g9: Circle CenterX=-23.5 CenterY=-23.5 CenterZ=0 NormalX=0 NormalY=0 NormalZ=1 AngleXU=0 Radius=2.5
    g10: LineSegment StartX=-32.1207 StartY=46 StartZ=0 EndX=-32.1207 EndY=-33.5 EndZ=0
    g11: LineSegment StartX=-32.1207 StartY=-33.5 StartZ=0 EndX=32.1207 EndY=-33.5 EndZ=0
    g12: LineSegment StartX=32.1207 StartY=-33.5 StartZ=0 EndX=32.1207 EndY=46 EndZ=0
    g13: LineSegment StartX=32.1207 StartY=46 StartZ=0 EndX=-32.1207 EndY=46 EndZ=0
    g14: GeomPoint [constr] X=0 Y=6.25 Z=0
    g15: LineSegment [constr] StartX=-27.7523 StartY=38.4474 StartZ=0 EndX=27.7523 EndY=38.4474 EndZ=0
    g16: Circle CenterX=-27.7523 CenterY=38.4474 CenterZ=0 NormalX=0 NormalY=0 NormalZ=1 AngleXU=0 Radius=2.5
    g17: Circle CenterX=0 CenterY=38.4474 CenterZ=0 NormalX=0 NormalY=0 NormalZ=1 AngleXU=0 Radius=2.5
    g18: Circle CenterX=27.7523 CenterY=38.4474 CenterZ=0 NormalX=0 NormalY=0 NormalZ=1 AngleXU=0 Radius=2.5
  constraints (39):
    c: Coincident(g0,g-1)
    c: Coincident(g1,g2)
    c: Coincident(g2,g3)
    c: Coincident(g3,g4)
    c: Coincident(g4,g1)
    c: Horizontal(g1)
    c: Horizontal(g3)
    c: Vertical(g2)
    c: Vertical(g4)
    c: Symmetric(g3,g1,g5)
    c: Coincident(g5,g0)
    c: Coincident(g7,g2)
    c: Coincident(g8,g1)
    c: Coincident(g9,g1)
    c: Coincident(g3,g6)
    c: Equal(g1,g2)
    c: Equal(g8,g9)
    c: Equal(g9,g6)
    c: Equal(g6,g7)
    c: Coincident(g10,g11)
    c: Coincident(g11,g12)
    c: Coincident(g12,g13)
    c: Coincident(g13,g10)
    c: Vertical(g10)
    c: Vertical(g12)
    c: Horizontal(g11)
    c: Horizontal(g13)
    c: Symmetric(g12,g10,g14)
    c: PointOnObject(g14,g-2)
    c: DistanceY(g10,g1) = 10
    c: DistanceX(g3,g3) = 47
    c: Diameter(g0) = 40
    c: DistanceY(g2,g12) = 22.5
    c: Diameter(g7) = 5
    c: Symmetric(g15,g15,g-2)
    c: Diameter(g16) = 5
    c: Coincident(g16,g15)
    c: Diameter(g17) = 5
    c: Diameter(g18) = 5
FEATURE [Sketcher::SketchObject] Sketch017
  ArcFitTolerance = 1e-06
  AttachmentSupport = -> [XY_Plane016]
  FullyConstrained = false
  MakeInternals = false
  MapMode = 5
  expr: Constraints[6] = <<ss>>.rf
  sketch-geometry (14):
    g0: LineSegment StartX=0 StartY=10 StartZ=0 EndX=200 EndY=10 EndZ=0
    g1: LineSegment [constr] StartX=0 StartY=-10 StartZ=0 EndX=0 EndY=8.25863 EndZ=0
    g2: LineSegment StartX=0 StartY=-10 StartZ=0 EndX=200 EndY=-10 EndZ=0
    g3: Circle [constr] CenterX=0 CenterY=0 CenterZ=0 NormalX=0 NormalY=0 NormalZ=1 AngleXU=0 Radius=4
    g4: Circle CenterX=200 CenterY=7e-16 CenterZ=0 NormalX=0 NormalY=0 NormalZ=1 AngleXU=0 Radius=4
    g5: ArcOfCircle CenterX=200 CenterY=7e-16 CenterZ=0 NormalX=0 NormalY=0 NormalZ=1 AngleXU=0 Radius=10 StartAngle=4.71239 EndAngle=7.85398
    g6: LineSegment StartX=0 StartY=10 StartZ=0 EndX=-12.4262 EndY=10 EndZ=0
    g7: LineSegment StartX=-12.4262 StartY=-10 StartZ=0 EndX=0 EndY=-10 EndZ=0
    g8: ArcOfCircle CenterX=0 CenterY=0 CenterZ=0 NormalX=0 NormalY=0 NormalZ=1 AngleXU=0 Radius=4 StartAngle=3.45389 EndAngle=9.11248
    g9: LineSegment StartX=-12.4262 StartY=-10 StartZ=0 EndX=-12.4262 EndY=-1.22899 EndZ=0
    g10: LineSegment StartX=-12.4262 StartY=-1.22899 StartZ=0 EndX=-3.80652 EndY=-1.22899 EndZ=0
    g11: LineSegment StartX=-12.4262 StartY=10 StartZ=0 EndX=-12.4262 EndY=1.22899 EndZ=0
    g12: LineSegment StartX=-12.4262 StartY=1.22899 StartZ=0 EndX=-3.80652 EndY=1.22899 EndZ=0
    g13: LineSegment [constr] StartX=-3.80652 StartY=1.22899 StartZ=0 EndX=-3.80652 EndY=-1.22899 EndZ=0
  constraints (36):
    c: Vertical(g1)
    c: Horizontal(g2)
    c: Parallel(g0,g2)
    c: Vertical(g0,g2)
    c: DistanceY(g1,g0) = 20
    c: Vertical(g2,g4)
    c: DistanceX(g3,g4) = 200
    c: Coincident(g0,g5)
    c: Coincident(g2,g5)
    c: Coincident(g4,g5)
    c: Diameter(g4) = 8
    c: Diameter(g3) = 8
    c: Coincident(g0,g6)
    c: Horizontal(g6)
    c: Coincident(g7,g2)
    c: Horizontal(g7)
    c: Symmetric(g0,g1,g3)
    c: Coincident(g3,g-1)
    c: PointOnObject(g0,g-2)
    c: Coincident(g1,g2)
    c: Coincident(g8,g3)
    c: PointOnObject(g8,g3)
    c: Coincident(g7,g9)
    c: Vertical(g9)
    c: Coincident(g9,g10)
    c: Coincident(g10,g8)
    c: Horizontal(g10)
    c: Coincident(g6,g11)
    c: Vertical(g11)
    c: Coincident(g11,g12)
    c: Coincident(g12,g8)
    c: Horizontal(g12)
    c: Equal(g9,g11)
    c: Equal(g12,g10)
    c: Coincident(g13,g8)
    c: Coincident(g13,g8)
FEATURE [PartDesign::Pad] Pad010
  Direction = (0,0,1)
  Length = 10
  Length2 = 10
  Profile = -> Sketch017
  ReferenceAxis = -> Sketch017 [N_Axis]
  Refine = true
  Suppressed = false
  Type = 0
FEATURE [Sketcher::SketchObject] Sketch019
  ArcFitTolerance = 1e-06
  AttachmentSupport = -> [Pad010]
  ExternalGeometry = -> [Pad010]
  FullyConstrained = true
  MakeInternals = false
  MapMode = 5
  Placement = pos=(0,10,0) rot=(0,0.707107,0.707107;3.14159rad)
  sketch-geometry (2):
    g0: Circle CenterX=7.42617 CenterY=5 CenterZ=0 NormalX=0 NormalY=0 NormalZ=1 AngleXU=0 Radius=2.5
    g1: LineSegment [constr] StartX=12.4262 StartY=5 StartZ=0 EndX=7.42617 EndY=5 EndZ=0
  constraints (5):
    c: Symmetric(g-3,g-3,g1)
    c: Coincident(g1,g0)
    c: Horizontal(g1)
    c: Distance(g1,g1) = 5
    c: Diameter(g0) = 5
FEATURE [PartDesign::Pad] Pad009
  Direction = (0,0,1)
  Length = 5
  Length2 = 10
  Profile = -> Sketch016
  ReferenceAxis = -> Sketch016 [N_Axis]
  Refine = true
  Suppressed = false
  Type = 0
FEATURE [PartDesign::Hole] Hole
  BaseFeature = -> Pad010
  CustomThreadClearance = 0
  Depth = 451.419
  DepthType = 1
  Diameter = 4.2
  DrillForDepth = false
  DrillPoint = 1
  DrillPointAngle = 118
  HoleCutCountersinkAngle = 90
  HoleCutCustomValues = false
  HoleCutDepth = 5
  HoleCutDiameter = 6
  HoleCutType = 1
  ModelThread = false
  Profile = -> Sketch019
  Refine = true
  Suppressed = false
  Tapered = false
  TaperedAngle = 90
  ThreadClass = 0
  ThreadDepth = 451.419
  ThreadDepthType = 0
  ThreadDirection = 0
  ThreadFit = 0
  ThreadSize = 13
  ThreadType = 1
  Threaded = true
  UseCustomThreadClearance = false
FEATURE [PartDesign::Body] Body008  label="bicep001"
  AllowCompound = false
  Group = -> [Sketch017,Pad010,Sketch019,Hole]
  Origin = -> Origin028
  Tip = -> Hole
FEATURE [App::Part] Part  label="bicep"
  Group = -> [Body008]
  Origin = -> Origin008
FEATURE [PartDesign::Chamfer] Chamfer001
  Angle = 45
  Base = -> Pad009 [Edge2,Edge5]
  BaseFeature = -> Pad009
  ChamferType = 0
  FlipDirection = false
  Refine = true
  Size = 5
  Size2 = 1
  SupportTransform = false
  Suppressed = false
  UseAllEdges = false
FEATURE [PartDesign::Body] Body007  label="nema23_holder"
  AllowCompound = false
  Group = -> [Sketch016,Pad009,Chamfer001]
  Origin = -> Origin026
  Tip = -> Chamfer001
FEATURE [PartDesign::Pad] Pad
  Direction = (0,0,1)
  Length = 400
  Length2 = 10
  Midplane = true
  Profile = -> Sketch
  ReferenceAxis = -> Sketch [N_Axis]
  Suppressed = false
  Type = 0
  expr: Length = Spreadsheet.re
FEATURE [PartDesign::Body] Body  label="forearm_axis"
  AllowCompound = false
  Group = -> [Sketch,Pad,Sketch010]
  Origin = -> Origin
  Tip = -> Pad
FEATURE [App::Part] Part001  label="forearm"
  Group = -> [Body]
  Origin = -> Origin009
FEATURE [Sketcher::SketchObject] Sketch020
  ArcFitTolerance = 1e-06
  AttachmentSupport = -> [PolarPattern]
  ExternalGeometry = -> [PolarPattern]
  FullyConstrained = false
  MakeInternals = false
  MapMode = 5
  Placement = pos=(0,0,10) rot=(0,0,1;0rad)
  sketch-geometry (35):
    g0: GeomPoint [constr] X=0 Y=0 Z=0
    g1: Circle CenterX=-5.70397 CenterY=9.87956 CenterZ=0 NormalX=0 NormalY=0 NormalZ=1 AngleXU=0 Radius=1.5
    g2: Circle CenterX=0 CenterY=0 CenterZ=0 NormalX=0 NormalY=0 NormalZ=1 AngleXU=0 Radius=1.5
    g3: Circle CenterX=11.4079 CenterY=0 CenterZ=0 NormalX=0 NormalY=0 NormalZ=1 AngleXU=0 Radius=1.5
    g4: Circle CenterX=-5.70397 CenterY=-9.87956 CenterZ=0 NormalX=0 NormalY=0 NormalZ=1 AngleXU=0 Radius=1.5
    g5: LineSegment [constr] StartX=5.70397 StartY=-9.87956 StartZ=0 EndX=5.70397 EndY=9.87956 EndZ=0
    g6: LineSegment [constr] StartX=5.70397 StartY=9.87956 StartZ=0 EndX=-11.4079 EndY=0 EndZ=0
    g7: LineSegment [constr] StartX=-11.4079 StartY=0 StartZ=0 EndX=5.70397 EndY=-9.87956 EndZ=0
    g8: Circle [constr] CenterX=0 CenterY=0 CenterZ=0 NormalX=0 NormalY=0 NormalZ=1 AngleXU=0 Radius=11.4079
    g9: LineSegment [constr] StartX=0 StartY=0 StartZ=0 EndX=-28.1472 EndY=48.7524 EndZ=0
    g10: Circle [constr] CenterX=0 CenterY=0 CenterZ=0 NormalX=0 NormalY=0 NormalZ=1 AngleXU=0 Radius=40
    g11: LineSegment [constr] StartX=0 StartY=0 StartZ=0 EndX=20 EndY=34.641 EndZ=0
    g12: LineSegment [constr] StartX=0 StartY=0 StartZ=0 EndX=20 EndY=-34.641 EndZ=0
    g13: LineSegment [constr] StartX=0 StartY=0 StartZ=0 EndX=-40 EndY=0 EndZ=0
    g14: GeomPoint [constr] X=-12.1812 Y=21.0985 Z=0
    g15: ArcOfCircle CenterX=-40 CenterY=2e-16 CenterZ=0 NormalX=0 NormalY=0 NormalZ=1 AngleXU=0 Radius=2.5 StartAngle=1.5708 EndAngle=4.71239
    g16: ArcOfCircle CenterX=-11.4079 CenterY=0 CenterZ=0 NormalX=0 NormalY=0 NormalZ=1 AngleXU=0 Radius=2.5 StartAngle=4.71239 EndAngle=7.85398
    g17: LineSegment StartX=-40 StartY=2.5 StartZ=0 EndX=-11.4079 EndY=2.5 EndZ=0
    g18: LineSegment StartX=-40 StartY=-2.5 StartZ=0 EndX=-11.4079 EndY=-2.5 EndZ=0
    g19: ArcOfCircle CenterX=5.70397 CenterY=-9.87956 CenterZ=0 NormalX=0 NormalY=0 NormalZ=1 AngleXU=0 Radius=2.5 StartAngle=0.523599 EndAngle=3.66519
    g20: ArcOfCircle CenterX=20 CenterY=-34.641 CenterZ=0 NormalX=0 NormalY=0 NormalZ=1 AngleXU=0 Radius=2.5 StartAngle=3.66519 EndAngle=6.80678
    g21: LineSegment StartX=7.86903 StartY=-8.62956 StartZ=0 EndX=22.1651 EndY=-33.391 EndZ=0
    g22: LineSegment StartX=3.5389 StartY=-11.1296 StartZ=0 EndX=17.8349 EndY=-35.891 EndZ=0
    g23: ArcOfCircle CenterX=5.70397 CenterY=9.87956 CenterZ=0 NormalX=0 NormalY=0 NormalZ=1 AngleXU=0 Radius=2.5 StartAngle=2.61799 EndAngle=5.75959
    g24: ArcOfCircle CenterX=20 CenterY=34.641 CenterZ=0 NormalX=0 NormalY=0 NormalZ=1 AngleXU=0 Radius=2.5 StartAngle=5.75959 EndAngle=8.90118
    g25: LineSegment StartX=3.5389 StartY=11.1296 StartZ=0 EndX=17.8349 EndY=35.891 EndZ=0
    g26: LineSegment StartX=7.86903 StartY=8.62956 StartZ=0 EndX=22.1651 EndY=33.391 EndZ=0
    g27: Circle [constr] CenterX=0 CenterY=0 CenterZ=0 NormalX=0 NormalY=0 NormalZ=1 AngleXU=0 Radius=11.4079
    g28: LineSegment [constr] StartX=5.70397 StartY=9.87956 StartZ=0 EndX=-5.70397 EndY=-9.87956 EndZ=0
    g29: Circle [constr] CenterX=20 CenterY=34.641 CenterZ=0 NormalX=0 NormalY=0 NormalZ=1 AngleXU=0 Radius=2.5
    g30: Circle [constr] CenterX=5.70397 CenterY=9.87956 CenterZ=0 NormalX=0 NormalY=0 NormalZ=1 AngleXU=0 Radius=2.5
    g31: Circle CenterX=-11.4079 CenterY=0 CenterZ=0 NormalX=0 NormalY=0 NormalZ=1 AngleXU=0 Radius=1e-16
    g32: Circle [constr] CenterX=-11.4079 CenterY=0 CenterZ=0 NormalX=0 NormalY=0 NormalZ=1 AngleXU=0 Radius=2.5
    g33: Circle [constr] CenterX=5.70397 CenterY=-9.87956 CenterZ=0 NormalX=0 NormalY=0 NormalZ=1 AngleXU=0 Radius=2.5
    g34: Circle [constr] CenterX=-40 CenterY=0 CenterZ=0 NormalX=0 NormalY=0 NormalZ=1 AngleXU=0 Radius=2.5
  constraints (77):
    c: Coincident(g0,g-1)
    c: Diameter(g1) = 3
    c: Diameter(g2) = 3
    c: Diameter(g3) = 3
    c: Diameter(g4) = 3
    c: Coincident(g5,g6)
    c: Coincident(g6,g7)
    c: Coincident(g7,g5)
    c: Equal(g5,g6)
    c: Equal(g5,g7)
    c: PointOnObject(g5,g8)
    c: PointOnObject(g6,g8)
    c: PointOnObject(g7,g8)
    c: Coincident(g8,g0)
    c: Coincident(g9,g0)
    c: Parallel(g-3,g9)
    c: Coincident(g10,g0)
    c: Coincident(g11,g0)
    c: PointOnObject(g11,g10)
    c: PointOnObject(g5,g11)
    c: Coincident(g12,g0)
    c: PointOnObject(g12,g10)
    c: PointOnObject(g5,g12)
    c: Coincident(g13,g0)
    c: PointOnObject(g13,g10)
    c: Horizontal(g13)
    c: PointOnObject(g6,g13)
    c: PointOnObject(g14,g9)
    c: Tangent(g15,g17) = 1.5708
    c: Tangent(g15,g18) = -1.5708
    c: Tangent(g16,g17) = 1.5708
    c: Tangent(g16,g18) = -1.5708
    c: Equal(g15,g16)
    c: Horizontal(g18)
    c: Tangent(g19,g21) = 1.5708
    c: Tangent(g19,g22) = -1.5708
    c: Tangent(g20,g21) = 1.5708
    c: Tangent(g20,g22) = -1.5708
    c: Equal(g19,g20)
    c: Coincident(g19,g5)
    c: Coincident(g20,g12)
    c: Tangent(g23,g25) = 1.5708
    c: Tangent(g23,g26) = -1.5708
    c: Tangent(g24,g25) = 1.5708
    c: Tangent(g24,g26) = -1.5708
    c: Equal(g23,g24)
    c: Coincident(g23,g5)
    c: Coincident(g24,g11)
    c: Equal(g24,g15)
    c: Equal(g15,g20)
    c: Radius(g24) = 2.5
    c: PointOnObject(g15,g10)
    c: Coincident(g2,g0)
    c: PointOnObject(g1,g9)
    c: Coincident(g6,g16)
    c: PointOnObject(g3,g-1)
    c: Coincident(g27,g0)
    c: PointOnObject(g1,g27)
    c: PointOnObject(g3,g27)
    c: PointOnObject(g4,g27)
    c: Coincident(g28,g5)
    c: Coincident(g28,g4)
    c: PointOnObject(g0,g28)
    c: PointOnObject(g6,g27)
    c: Coincident(g29,g11)
    c: PointOnObject(g24,g29)
    c: Coincident(g30,g5)
    c: PointOnObject(g23,g30)
    c: Coincident(g31,g6)
    c: Tangent(g31,g8)
    c: Coincident(g32,g6)
    c: PointOnObject(g16,g32)
    c: Coincident(g33,g5)
    c: PointOnObject(g19,g33)
    c: Coincident(g34,g13)
    c: PointOnObject(g15,g34)
    c: Diameter(g10) = 80
FEATURE [PartDesign::Pocket] Pocket
  BaseFeature = -> PolarPattern
  Direction = (0,0,-1)
  Length = 5
  Length2 = 5
  Profile = -> Sketch020
  ReferenceAxis = -> Sketch020 [N_Axis]
  Refine = true
  Suppressed = false
  Type = 1
FEATURE [Sketcher::SketchObject] Sketch021
  ArcFitTolerance = 1e-06
  AttachmentSupport = -> [XY_Plane017]
  FullyConstrained = false
  MakeInternals = false
  MapMode = 5
  expr: Constraints[19] = <<ss>>.wrist / 10
  sketch-geometry (22):
    g0: Circle [constr] CenterX=0 CenterY=0 CenterZ=0 NormalX=0 NormalY=0 NormalZ=1 AngleXU=0 Radius=44.8482
    g1: LineSegment [constr] StartX=-77.6793 StartY=44.8482 StartZ=0 EndX=0 EndY=-89.6963 EndZ=0
    g2: LineSegment [constr] StartX=0 StartY=-89.6963 StartZ=0 EndX=77.6793 EndY=44.8482 EndZ=0
    g3: LineSegment [constr] StartX=77.6793 StartY=44.8482 StartZ=0 EndX=-77.6793 EndY=44.8482 EndZ=0
    g4: Circle [constr] CenterX=0 CenterY=0 CenterZ=0 NormalX=0 NormalY=0 NormalZ=1 AngleXU=0 Radius=89.6963
    g5: LineSegment StartX=-31.3396 StartY=-35.4145 StartZ=0 EndX=-46.3396 EndY=-9.4337 EndZ=0
    g6: LineSegment StartX=-15 StartY=44.8482 StartZ=0 EndX=15 EndY=44.8482 EndZ=0
    g7: Circle CenterX=0 CenterY=0 CenterZ=0 NormalX=0 NormalY=0 NormalZ=1 AngleXU=0 Radius=4.5
    g8: LineSegment StartX=31.3396 StartY=-35.4145 StartZ=0 EndX=46.3396 EndY=-9.4337 EndZ=0
    g9: LineSegment StartX=15 StartY=44.8482 StartZ=0 EndX=15 EndY=8.66025 EndZ=0
    g10: LineSegment StartX=15 StartY=8.66025 StartZ=0 EndX=46.3396 EndY=-9.4337 EndZ=0
    g11: LineSegment StartX=-31.3396 StartY=-35.4145 StartZ=0 EndX=0 EndY=-17.3205 EndZ=0
    g12: LineSegment StartX=0 StartY=-17.3205 StartZ=0 EndX=31.3396 EndY=-35.4145 EndZ=0
    g13: LineSegment StartX=-46.3396 StartY=-9.4337 StartZ=0 EndX=-15 EndY=8.66025 EndZ=0
    g14: LineSegment StartX=-15 StartY=8.66025 StartZ=0 EndX=-15 EndY=44.8482 EndZ=0
    g15: Circle CenterX=0 CenterY=17.3205 CenterZ=0 NormalX=0 NormalY=0 NormalZ=1 AngleXU=0 Radius=1.5
    g16: Circle CenterX=15 CenterY=-8.66025 CenterZ=0 NormalX=0 NormalY=0 NormalZ=1 AngleXU=0 Radius=1.5
    g17: Circle CenterX=-15 CenterY=-8.66025 CenterZ=0 NormalX=0 NormalY=0 NormalZ=1 AngleXU=0 Radius=1.5
    g18: LineSegment [constr] StartX=0 StartY=17.3205 StartZ=0 EndX=-15 EndY=-8.66025 EndZ=0
    g19: LineSegment [constr] StartX=-15 StartY=-8.66025 StartZ=0 EndX=15 EndY=-8.66025 EndZ=0
    g20: LineSegment [constr] StartX=15 StartY=-8.66025 StartZ=0 EndX=0 EndY=17.3205 EndZ=0
    g21: Circle [constr] CenterX=0 CenterY=0 CenterZ=0 NormalX=0 NormalY=0 NormalZ=1 AngleXU=0 Radius=17.3205
  constraints (59):
    c: Coincident(g0,g-1)
    c: Coincident(g1,g2)
    c: Coincident(g2,g3)
    c: Coincident(g3,g1)
    c: Equal(g1,g2)
    c: Equal(g1,g3)
    c: PointOnObject(g1,g4)
    c: PointOnObject(g2,g4)
    c: PointOnObject(g3,g4)
    c: Tangent(g3,g0)
    c: PointOnObject(g5,g1)
    c: PointOnObject(g6,g3)
    c: PointOnObject(g8,g2)
    c: PointOnObject(g6,g3)
    c: PointOnObject(g5,g1)
    c: PointOnObject(g8,g2)
    c: Horizontal(g3)
    c: Coincident(g0,g4)
    c: Coincident(g7,g0)
    c: Diameter(g7) = 9
    c: Distance(g8,g8) = 30
    c: Coincident(g6,g9)
    c: Coincident(g9,g10)
    c: Coincident(g10,g8)
    c: Coincident(g5,g11)
    c: Coincident(g11,g12)
    c: Coincident(g12,g8)
    c: Coincident(g5,g13)
    c: Coincident(g13,g14)
    c: Coincident(g14,g6)
    c: Equal(g14,g13)
    c: Equal(g13,g11)
    c: Equal(g11,g12)
    c: Equal(g9,g10)
    c: Equal(g10,g12)
    c: Perpendicular(g8,g10)
    c: Perpendicular(g6,g9)
    c: Perpendicular(g5,g13)
    c: Perpendicular(g6,g14)
    c: Perpendicular(g11,g5)
    c: PointOnObject(g15,g-2)
    c: Coincident(g18,g19)
    c: Coincident(g19,g20)
    c: Coincident(g20,g18)
    c: Equal(g18,g19)
    c: Equal(g18,g20)
    c: PointOnObject(g18,g21)
    c: PointOnObject(g19,g21)
    c: PointOnObject(g20,g21)
    c: Coincident(g21,g0)
    c: Coincident(g20,g15)
    c: Coincident(g16,g19)
    c: Coincident(g17,g18)
    c: Equal(g17,g16)
    c: Equal(g16,g15)
    c: Diameter(g15) = 3
    c: PointOnObject(g11,g-2)
    c: DistanceX(g3,g3) = 155.359
    c: Distance(g20,g20) = 30
FEATURE [PartDesign::Pad] Pad011
  Direction = (0,0,1)
  Length = 10
  Length2 = 10
  Profile = -> Sketch021
  ReferenceAxis = -> Sketch021 [N_Axis]
  Refine = true
  Suppressed = false
  Type = 0
FEATURE [PartDesign::Fillet] Fillet
  Base = -> Pad011 [Edge15,Edge24,Edge6,Edge25,Edge7,Edge16]
  BaseFeature = -> Pad011
  Radius = 4.5
  Refine = true
  SupportTransform = false
  Suppressed = false
  UseAllEdges = false
FEATURE [Sketcher::SketchObject] Sketch023
  ArcFitTolerance = 1e-06
  AttachmentSupport = -> [YZ_Plane018]
  FullyConstrained = true
  MakeInternals = false
  MapMode = 5
  Placement = pos=(0,0,0) rot=(0.57735,0.57735,0.57735;2.0944rad)
  expr: Constraints[11] = 26 / 2
  sketch-geometry (4):
    g0: LineSegment StartX=3.1 StartY=0 StartZ=0 EndX=3.1 EndY=13 EndZ=0
    g1: LineSegment StartX=3.1 StartY=13 StartZ=0 EndX=4.1 EndY=13 EndZ=0
    g2: LineSegment StartX=4.1 StartY=13 StartZ=0 EndX=6 EndY=0 EndZ=0
    g3: LineSegment StartX=6 StartY=0 StartZ=0 EndX=3.1 EndY=0 EndZ=0
  constraints (12):
    c: PointOnObject(g0,g-1)
    c: Vertical(g0)
    c: Coincident(g0,g1)
    c: Coincident(g1,g2)
    c: PointOnObject(g2,g-1)
    c: Coincident(g2,g3)
    c: Coincident(g3,g0)
    c: Horizontal(g1)
    c: Distance(g1,g1) = 1
    c: DistanceX(g-1,g2) = 6
    c: Distance(g-1,g0) = 3.1
    c: DistanceY(g0,g0) = 13
FEATURE [PartDesign::Revolution] Revolution
  Angle = 360
  Angle2 = 60
  Axis = (0,0,1)
  Base = (0,0,0)
  Placement = pos=(0,0,0) rot=(1,1,1;2.0944rad)
  Profile = -> Sketch023
  ReferenceAxis = -> Sketch023 [V_Axis]
  Refine = true
  Reversed = true
  Suppressed = false
  Type = 0
FEATURE [PartDesign::Body] Body010  label="cone_spacer"
  AllowCompound = false
  Group = -> [Sketch023,Revolution]
  Origin = -> Origin040
  Tip = -> Revolution
FEATURE [Sketcher::SketchObject] Sketch022
  ArcFitTolerance = 1e-06
  AttachmentSupport = -> [YZ_Plane017]
  ExternalGeometry = -> [Fillet]
  FullyConstrained = false
  MakeInternals = false
  MapMode = 5
  Placement = pos=(0,0,0) rot=(0.57735,0.57735,0.57735;2.0944rad)
  sketch-geometry (2):
    g0: Circle CenterX=39.8482 CenterY=5 CenterZ=0 NormalX=0 NormalY=0 NormalZ=1 AngleXU=0 Radius=3
    g1: LineSegment [constr] StartX=29.5949 StartY=5 StartZ=0 EndX=44.8482 EndY=5 EndZ=0
  constraints (5):
    c: Diameter(g0) = 6
    c: Symmetric(g-3,g-4,g1)
    c: PointOnObject(g0,g1)
    c: Vertical(g1,g-4)
    c: DistanceX(g0,g1) = 5
FEATURE [PartDesign::Pocket] Pocket004
  BaseFeature = -> Fillet
  Direction = (-1,0,0)
  Length = 5
  Length2 = 5
  Midplane = true
  Profile = -> Sketch022
  ReferenceAxis = -> Sketch022 [N_Axis]
  Refine = true
  Suppressed = false
  Type = 1
FEATURE [PartDesign::PolarPattern] PolarPattern001
  Angle = 360
  Axis = -> Sketch022 [V_Axis]
  BaseFeature = -> Pocket004
  Mode = 0
  Occurrences = 3
  Offset = 120
  Originals = -> [Pocket004]
  Refine = true
  Suppressed = false
  TransformMode = 0
FEATURE [PartDesign::Fillet] Fillet001
  Base = -> PolarPattern001 [Edge52,Edge43,Edge6]
  BaseFeature = -> PolarPattern001
  Radius = 45
  Refine = true
  SupportTransform = false
  Suppressed = false
  UseAllEdges = false
FEATURE [Part::Part2DObjectPython] Shape2DView  # Draft 2D object (typed FeaturePython)
  AutoUpdate = true
  Base = -> Pocket
  Clip = false
  FuseArch = false
  HiddenLines = false
  InPlace = true
  OnlySolids = false
  Projection = (0,0,1)
  ProjectionMode = 0
  SegmentLength = 0.05
  Tessellation = false
  VisibleOnly = false
FEATURE [Sketcher::SketchObject] Sketch024
  ArcFitTolerance = 1e-06
  AttachmentSupport = -> [XY_Plane012]
  ExternalGeometry = -> [Pocket]
  FullyConstrained = true
  MakeInternals = false
  MapMode = 5
  sketch-geometry (18):
    g0: LineSegment [constr] StartX=-179.382 StartY=80.7711 StartZ=0 EndX=-179.382 EndY=40.7711 EndZ=0
    g1: LineSegment [constr] StartX=-179.382 StartY=40.7711 StartZ=0 EndX=70.6176 EndY=40.7711 EndZ=0
    g2: LineSegment [constr] StartX=70.6176 StartY=40.7711 StartZ=0 EndX=70.6176 EndY=80.7711 EndZ=0
    g3: LineSegment [constr] StartX=70.6176 StartY=80.7711 StartZ=0 EndX=-179.382 EndY=80.7711 EndZ=0
    g4: LineSegment [constr] StartX=-70.6176 StartY=40.7711 StartZ=0 EndX=54.3824 EndY=-175.735 EndZ=0
    g5: LineSegment [constr] StartX=54.3824 StartY=-175.735 StartZ=0 EndX=19.7414 EndY=-195.735 EndZ=0
    g6: LineSegment [constr] StartX=19.7414 StartY=-195.735 StartZ=0 EndX=-105.259 EndY=20.7711 EndZ=0
    g7: LineSegment [constr] StartX=-105.259 StartY=20.7711 StartZ=0 EndX=-70.6176 EndY=40.7711 EndZ=0
    g8: LineSegment [constr] StartX=45.7221 StartY=-180.735 StartZ=0 EndX=-79.2779 EndY=35.7711 EndZ=0
    g9: LineSegment [constr] StartX=125 StartY=134.964 StartZ=0 EndX=-2.84e-14 EndY=-81.5422 EndZ=0
    g10: LineSegment [constr] StartX=-2.84e-14 StartY=-81.5422 StartZ=0 EndX=8.66025 EndY=-86.5422 EndZ=0
    g11: LineSegment [constr] StartX=8.66025 StartY=-86.5422 StartZ=0 EndX=133.66 EndY=129.964 EndZ=0
    g12: LineSegment [constr] StartX=133.66 StartY=129.964 StartZ=0 EndX=125 EndY=134.964 EndZ=0
    g13: GeomPoint [constr] X=-156.232 Y=20.7711 Z=0
    g14: LineSegment [constr] StartX=-156.232 StartY=270.602 StartZ=0 EndX=-156.232 EndY=-270.602 EndZ=0
    g15: LineSegment [constr] StartX=-156.232 StartY=-270.602 StartZ=0 EndX=312.465 EndY=0 EndZ=0
    g16: LineSegment [constr] StartX=312.465 StartY=0 StartZ=0 EndX=-156.232 EndY=270.602 EndZ=0
    g17: Circle [constr] CenterX=0 CenterY=0 CenterZ=0 NormalX=0 NormalY=0 NormalZ=1 AngleXU=0 Radius=312.465
  constraints (54):
    c: Coincident(g0,g1)
    c: Coincident(g1,g2)
    c: Vertical(g2)
    c: Coincident(g2,g3)
    c: Coincident(g3,g0)
    c: Horizontal(g3)
    c: Vertical(g0)
    c: DistanceY(g0,g-9) = 10
    c: Horizontal(g1)
    c: DistanceY(g0,g0) = 40
    c: DistanceX(g3,g3) = 250
    c: PointOnObject(g4,g1)
    c: Coincident(g4,g5)
    c: Coincident(g5,g6)
    c: Coincident(g6,g7)
    c: Coincident(g7,g4)
    c: Parallel(g-4,g4)
    c: Parallel(g6,g4)
    c: Perpendicular(g4,g5)
    c: Perpendicular(g4,g7)
    c: Distance(g5,g5) = 40
    c: PointOnObject(g8,g5)
    c: PointOnObject(g8,g7)
    c: Parallel(g8,g6)
    c: Distance(g4,g8) = 10
    c: Distance(g6,g6) = 250
    c: Distance(g9,g9) = 250
    c: Parallel(g-5,g9)
    c: PointOnObject(g1,g9)
    c: PointOnObject(g9,g4)
    c: PointOnObject(g-11,g8)
    c: Coincident(g9,g10)
    c: Coincident(g10,g11)
    c: Parallel(g11,g9)
    c: Perpendicular(g9,g10)
    c: Distance(g10,g10) = 10
    c: PointOnObject(g-6,g11)
    c: Equal(g11,g9)
    c: Coincident(g11,g12)
    c: Coincident(g12,g9)
    c: DistanceX(g0,g13) = 23.15
    c: DistanceY(g13,g0) = 20
    c: Coincident(g14,g15)
    c: Coincident(g15,g16)
    c: Coincident(g16,g14)
    c: Equal(g14,g15)
    c: Equal(g14,g16)
    c: PointOnObject(g14,g17)
    c: PointOnObject(g15,g17)
    c: PointOnObject(g16,g17)
    c: Coincident(g17,g-1)
    c: Vertical(g14)
    c: PointOnObject(g13,g14)
    c: Distance(g16,g16) = 541.205  'DELTA_F'
FEATURE [PartDesign::Body] Body004  label="base_triangle"
  AllowCompound = false
  Group = -> [Sketch011,Pad007,Sketch012,Pocket003,PolarPattern,Sketch020,Pocket,Sketch024]
  Origin = -> Origin012
  Tip = -> Pocket
FEATURE [App::Part] Part003  label="base"
  Group = -> [Body004]
  Origin = -> Origin011
FEATURE [Sketcher::SketchObject] Sketch025
  ArcFitTolerance = 1e-06
  AttachmentSupport = -> [Fillet001]
  ExternalGeometry = -> [Fillet001]
  FullyConstrained = false
  MakeInternals = false
  MapMode = 5
  Placement = pos=(0,0,10) rot=(0,0,1;0rad)
  sketch-geometry (3):
    g0: LineSegment [constr] StartX=-15 StartY=-8.66025 StartZ=0 EndX=48.1553 EndY=27.8025 EndZ=0
    g1: Circle CenterX=7.9174 CenterY=4.57111 CenterZ=0 NormalX=0 NormalY=0 NormalZ=1 AngleXU=0 Radius=1.4457
    g2: Circle CenterX=16.5777 CenterY=9.57111 CenterZ=0 NormalX=0 NormalY=0 NormalZ=1 AngleXU=0 Radius=1.4457
  constraints (6):
    c: Coincident(g0,g-4)
    c: PointOnObject(g-1,g0)
    c: PointOnObject(g1,g0)
    c: Symmetric(g0,g0,g2)
    c: Equal(g1,g2)
    c: Distance(g1,g2) = 10
FEATURE [PartDesign::Pocket] Pocket005
  BaseFeature = -> Fillet001
  Direction = (0,0,-1)
  Length = 5
  Length2 = 5
  Profile = -> Sketch025
  ReferenceAxis = -> Sketch025 [N_Axis]
  Refine = true
  Suppressed = false
  Type = 1
FEATURE [PartDesign::PolarPattern] PolarPattern002
  Angle = 360
  Axis = -> Sketch025 [N_Axis]
  BaseFeature = -> Pocket005
  Mode = 0
  Occurrences = 3
  Offset = 120
  Originals = -> [Pocket005]
  Refine = true
  Suppressed = false
  TransformMode = 0
FEATURE [PartDesign::Body] Body009  label="tool001"
  AllowCompound = false
  Group = -> [Sketch021,Pad011,Fillet,Sketch022,Pocket004,PolarPattern001,Fillet001,Sketch025,Pocket005,PolarPattern002]
  Origin = -> Origin039
  Tip = -> PolarPattern002
---- part stepper-motor-nema-23-57bygh201-1.snapshot.3/nema23.FCStd = doc fcstd_12693ea62d56 ----
FCSTD DOCUMENT  (FreeCAD 1.0R38641 +468 (Git))
Label: nema23
License: All rights reserved
LicenseURL: https://en.wikipedia.org/wiki/All_rights_reserved
objects: Part::Feature×5, Part::MultiFuse×2, App::Part×1
note: 7 computed .brp shape members not serialized (recipe doc carries the construction recipe); baked Part::Feature solids carry a one-line shape summary decoded from their .brp

FEATURE [Part::Feature] Part__Feature  label="Up"
  shape: bbox 56.4 x 56.4 x 12.6 mm, 78 faces (baked)
FEATURE [Part::Feature] Part__Feature001  label="Axe"
  shape: bbox 10 x 10 x 70.4 mm, 13 faces (baked)
FEATURE [Part::Feature] Part__Feature002  label="Bottom"
  shape: bbox 56.81 x 56.81 x 11.93 mm, 535 faces (baked)
FEATURE [Part::Feature] Part__Feature003  label="Middle"
  shape: bbox 56.4 x 56.4 x 31.5 mm, 27 faces (baked)
FEATURE [Part::Feature] Part__Feature008  label="Sticker"
  Placement = pos=(0,-28.2,-24.4) rot=(1,0,0;1.5708rad)
  shape: bbox 26 x 0.1 x 13 mm, 831 faces (baked)
FEATURE [Part::MultiFuse] Fusion
  Shapes = -> [Part__Feature008,Part__Feature003]
FEATURE [Part::MultiFuse] Fusion001
  Shapes = -> [Part__Feature008,Part__Feature003,Part__Feature,Part__Feature001,Part__Feature002,Fusion]
FEATURE [App::Part] nema23_57byg201
  Group = -> [Fusion,Part__Feature,Part__Feature003,Part__Feature001,Part__Feature002,Part__Feature008,Fusion001]
  Origin = -> Origin
